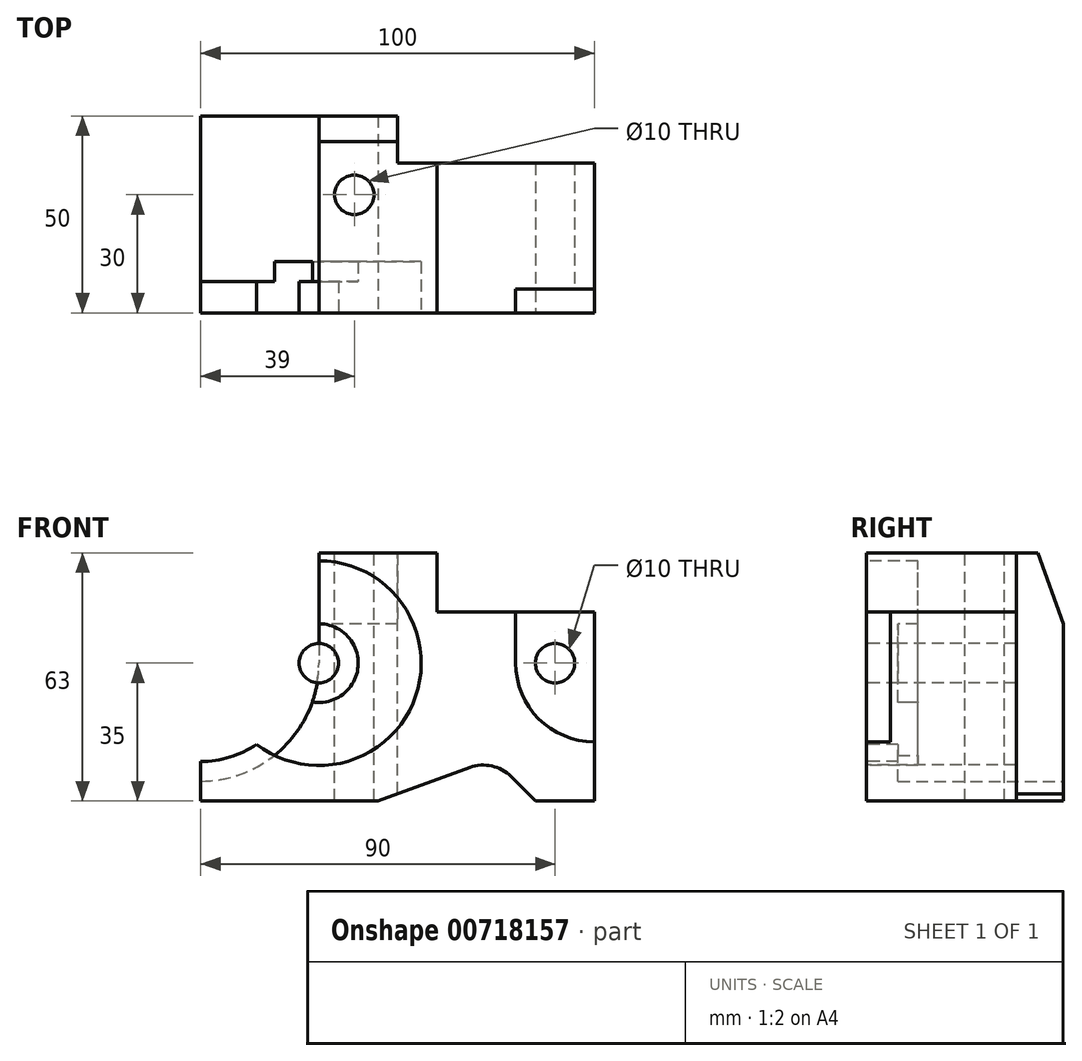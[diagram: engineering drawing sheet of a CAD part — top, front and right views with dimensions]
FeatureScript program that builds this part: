
annotation { "Feature Type Name" : "Feature", "Feature Type Description" : "" }
export const myFeature = defineFeature(function(context is Context, id is Id, definition is map)
    precondition{}
    {
        {
            var Q0;
            Q0=qCreatedBy(makeId("Front.planeOp"),FACE);
            var sketch = newSketch(context, id + "F0", { "sketchPlane" : qUnion([Q0])});
            skLineSegment(sketch, "E0.bottom", {"start": v(0, 0) * mm, "end": v(100, 0) * mm});
            skLineSegment(sketch, "E0.top", {"start": v(0, 63) * mm, "end": v(100, 63) * mm});
            skLineSegment(sketch, "E0.left", {"start": v(0, 0) * mm, "end": v(0, 63) * mm});
            skLineSegment(sketch, "E0.right", {"start": v(100, 0) * mm, "end": v(100, 63) * mm});
            skSolve(sketch);
        }
        {
            var Q0;
            Q0 = qSketchRegion(id + "F0", true);
            extrude(context, id + "F1", {"entities" : qUnion([Q0]), "depth" : 50 * mm, "offsetDistance" : 25 * mm});
        }
        {
            var Q0;
            Q0=makeQuery(id+"F1.opExtrude","CAP_FACE",FACE,{"disambiguationData":[OSD([sQuery(id+"F0.wireOp",EDGE,"E0.bottom"),sQuery(id+"F0.wireOp",EDGE,"E0.top"),sQuery(id+"F0.wireOp",EDGE,"E0.left"),sQuery(id+"F0.wireOp",EDGE,"E0.right")])],"isStart":false});
            var sketch = newSketch(context, id + "F2", { "sketchPlane" : qUnion([Q0])});
            skLineSegment(sketch, "E1.bottom", {"start": v(100, 63) * mm, "end": v(60, 63) * mm});
            skLineSegment(sketch, "E1.top", {"start": v(100, 48) * mm, "end": v(60, 48) * mm});
            skLineSegment(sketch, "E1.left", {"start": v(100, 63) * mm, "end": v(100, 48) * mm});
            skLineSegment(sketch, "E1.right", {"start": v(60, 63) * mm, "end": v(60, 48) * mm});
            skSolve(sketch);
        }
        {
            var Q0;
            Q0 = qSketchRegion(id + "F2", true);
            extrude(context, id + "F3", {"entities" : qUnion([Q0]), "operationType" : NewBodyOperationType.REMOVE, "endBound" : BoundingType.THROUGH_ALL, "oppositeDirection" : true, "depth" : 25 * mm, "offsetDistance" : 25 * mm});
        }
        {
            var Q0;
            Q0=makeQuery(id+"F1.opExtrude","CAP_FACE",FACE,{"disambiguationData":[OSD([sQuery(id+"F0.wireOp",EDGE,"E0.bottom"),sQuery(id+"F0.wireOp",EDGE,"E0.top"),sQuery(id+"F0.wireOp",EDGE,"E0.left"),sQuery(id+"F0.wireOp",EDGE,"E0.right")])],"isStart":false});
            var sketch = newSketch(context, id + "F4", { "sketchPlane" : qUnion([Q0])});
            skCircle(sketch, "E2", {"center": v(90, 35) * mm, "radius": 5 * mm});
            skSolve(sketch);
        }
        {
            var Q0;
            Q0 = qSketchRegion(id + "F4", true);
            extrude(context, id + "F5", {"entities" : qUnion([Q0]), "operationType" : NewBodyOperationType.REMOVE, "endBound" : BoundingType.THROUGH_ALL, "oppositeDirection" : true, "depth" : 25 * mm, "offsetDistance" : 25 * mm});
        }
        {
            var Q0;
            Q0=makeQuery(id+"F1.opExtrude","CAP_FACE",FACE,{"disambiguationData":[OSD([sQuery(id+"F0.wireOp",EDGE,"E0.bottom"),sQuery(id+"F0.wireOp",EDGE,"E0.top"),sQuery(id+"F0.wireOp",EDGE,"E0.left"),sQuery(id+"F0.wireOp",EDGE,"E0.right")])],"isStart":false});
            var sketch = newSketch(context, id + "F6", { "sketchPlane" : qUnion([Q0])});
            skLineSegment(sketch, "E3", {"start": v(45, 0) * mm, "end": v(68.34, 8.5) * mm});
            skArc(sketch, "E4", {"start": v(78.83, 6.17) * mm, "mid": v(73.92, 8.86) * mm, "end": v(68.34, 8.5) * mm});
            skLineSegment(sketch, "E5", {"start": v(78.83, 6.17) * mm, "end": v(85, 0) * mm});
            skLineSegment(sketch, "E6", {"start": v(45, 0) * mm, "end": v(85, 0) * mm});
            skSolve(sketch);
        }
        {
            var Q0;
            Q0 = qSketchRegion(id + "F6", true);
            extrude(context, id + "F7", {"entities" : qUnion([Q0]), "operationType" : NewBodyOperationType.REMOVE, "endBound" : BoundingType.THROUGH_ALL, "oppositeDirection" : true, "depth" : 25 * mm, "offsetDistance" : 25 * mm});
        }
        {
            var Q0;
            Q0=makeQuery(id+"F1.opExtrude","CAP_FACE",FACE,{"disambiguationData":[OSD([sQuery(id+"F0.wireOp",EDGE,"E0.bottom"),sQuery(id+"F0.wireOp",EDGE,"E0.top"),sQuery(id+"F0.wireOp",EDGE,"E0.left"),sQuery(id+"F0.wireOp",EDGE,"E0.right")])],"isStart":false});
            var sketch = newSketch(context, id + "F8", { "sketchPlane" : qUnion([Q0])});
            skLineSegment(sketch, "E7", {"start": v(80, 48) * mm, "end": v(80, 35) * mm});
            skArc(sketch, "E8", {"start": v(80, 35) * mm, "mid": v(85.86, 20.86) * mm, "end": v(100, 15) * mm});
            skLineSegment(sketch, "E9", {"start": v(80, 48) * mm, "end": v(100, 48) * mm});
            skLineSegment(sketch, "E10", {"start": v(100, 48) * mm, "end": v(100, 15) * mm});
            skSolve(sketch);
        }
        {
            var Q0;
            Q0 = qSketchRegion(id + "F8", true);
            extrude(context, id + "F9", {"entities" : qUnion([Q0]), "operationType" : NewBodyOperationType.REMOVE, "oppositeDirection" : true, "depth" : 6 * mm, "offsetDistance" : 25 * mm});
        }
        {
            var Q0;
            Q0=makeQuery(id+"F1.opExtrude","SWEPT_FACE",FACE,{"disambiguationData":[OSD([sQuery(id+"F0.wireOp",EDGE,"E0.top")])]});
            var sketch = newSketch(context, id + "F10", { "sketchPlane" : qUnion([Q0])});
            skLineSegment(sketch, "E11.bottom", {"start": v(50, 0) * mm, "end": v(100, 0) * mm});
            skLineSegment(sketch, "E11.top", {"start": v(50, -12) * mm, "end": v(100, -12) * mm});
            skLineSegment(sketch, "E11.left", {"start": v(50, 0) * mm, "end": v(50, -12) * mm});
            skLineSegment(sketch, "E11.right", {"start": v(100, 0) * mm, "end": v(100, -12) * mm});
            skSolve(sketch);
        }
        {
            var Q0;
            Q0 = qSketchRegion(id + "F10", true);
            extrude(context, id + "F11", {"entities" : qUnion([Q0]), "operationType" : NewBodyOperationType.REMOVE, "endBound" : BoundingType.THROUGH_ALL, "oppositeDirection" : true, "depth" : 25 * mm, "offsetDistance" : 25 * mm});
        }
        {
            var Q0;
            Q0=makeQuery(id+"F1.opExtrude","CAP_FACE",FACE,{"disambiguationData":[OSD([sQuery(id+"F0.wireOp",EDGE,"E0.bottom"),sQuery(id+"F0.wireOp",EDGE,"E0.top"),sQuery(id+"F0.wireOp",EDGE,"E0.left"),sQuery(id+"F0.wireOp",EDGE,"E0.right")])],"isStart":false});
            var sketch = newSketch(context, id + "F12", { "sketchPlane" : qUnion([Q0])});
            skCircle(sketch, "E12", {"center": v(30, 35) * mm, "radius": 26 * mm});
            skCircle(sketch, "E13", {"center": v(30, 35) * mm, "radius": 10 * mm});
            skSolve(sketch);
        }
        {
            var Q0;
            Q0 = qSketchRegion(id + "F12", true);
            extrude(context, id + "F13", {"entities" : qUnion([Q0]), "operationType" : NewBodyOperationType.REMOVE, "oppositeDirection" : true, "depth" : 13 * mm, "offsetDistance" : 25 * mm});
        }
        {
            var Q0;
            Q0=makeQuery(id+"F13.boolean.opBoolean","SPLIT",FACE,{"disambiguationData":[TD([makeQuery(id+"F13.opExtrude","SWEPT_FACE",FACE,{"disambiguationData":[OSD([sQuery(id+"F12.wireOp",EDGE,"E13")])]})])],"derivedFrom":makeQuery(id+"F1.opExtrude","CAP_FACE",FACE,{"disambiguationData":[OSD([sQuery(id+"F0.wireOp",EDGE,"E0.bottom"),sQuery(id+"F0.wireOp",EDGE,"E0.top"),sQuery(id+"F0.wireOp",EDGE,"E0.left"),sQuery(id+"F0.wireOp",EDGE,"E0.right")])],"isStart":false})});
            var sketch = newSketch(context, id + "F14", { "sketchPlane" : qUnion([Q0])});
            skCircle(sketch, "E14", {"center": v(30, 35) * mm, "radius": 5 * mm});
            skCircle(sketch, "E15", {"center": v(30, 35) * mm, "radius": 10 * mm});
            skSolve(sketch);
        }
        {
            var Q0;
            Q0 = qSketchRegion(id + "F14", true);
            extrude(context, id + "F15", {"entities" : qUnion([Q0]), "operationType" : NewBodyOperationType.REMOVE, "oppositeDirection" : true, "depth" : 8 * mm, "offsetDistance" : 25 * mm});
        }
        {
            var Q0;
            {var subQ0=sQuery(id+"F0.wireOp",EDGE,"E0.bottom");var subQ1=sQuery(id+"F0.wireOp",EDGE,"E0.right");var subQ2=sQuery(id+"F0.wireOp",EDGE,"E0.top");var subQ3=sQuery(id+"F0.wireOp",EDGE,"E0.left");Q0=makeQuery(id+"F13.boolean.opBoolean","SPLIT",FACE,{"disambiguationData":[TD([makeQuery(id+"F1.opExtrude","SWEPT_FACE",FACE,{"disambiguationData":[OSD([subQ0])]})])],"derivedFrom":makeQuery(id+"F1.opExtrude","CAP_FACE",FACE,{"disambiguationData":[OSD([subQ0,subQ2,subQ3,subQ1])],"isStart":false})});}
            var sketch = newSketch(context, id + "F16", { "sketchPlane" : qUnion([Q0])});
            skArc(sketch, "E16", {"start": v(0, 10) * mm, "mid": v(7.4, 11.12) * mm, "end": v(14.15, 14.39) * mm});
            skLineSegment(sketch, "E17", {"start": v(0, 10) * mm, "end": v(0, 35) * mm});
            skArc(sketch, "E18", {"start": v(30, 61) * mm, "mid": v(5.38, 43.37) * mm, "end": v(14.15, 14.39) * mm});
            skPoint(sketch, "E19.end.orphan", {"position": v(30, 63) * mm});
            skLineSegment(sketch, "E20", {"start": v(30, 63) * mm, "end": v(0, 63) * mm});
            skLineSegment(sketch, "E21", {"start": v(0, 63) * mm, "end": v(0, 35) * mm});
            skLineSegment(sketch, "E22", {"start": v(30, 61) * mm, "end": v(30, 63) * mm});
            skSolve(sketch);
        }
        {
            var Q0;
            Q0 = qSketchRegion(id + "F16", true);
            var Q1;
            Q1=makeQuery(id+"F13.boolean.opBoolean","COPY",FACE,{"derivedFrom":makeQuery(id+"F13.opExtrude","CAP_FACE",FACE,{"disambiguationData":[OSD([sQuery(id+"F12.wireOp",EDGE,"E12"),sQuery(id+"F12.wireOp",EDGE,"E13")])],"isStart":false})});
            extrude(context, id + "F17", {"entities" : qUnion([Q0]), "operationType" : NewBodyOperationType.REMOVE, "oppositeDirection" : true, "depth" : 8 * mm, "endBoundEntityFace" : qUnion([Q1]), "offsetDistance" : 25 * mm});
        }
        {
            var Q0;
            Q0=makeQuery(id+"F1.opExtrude","CAP_FACE",FACE,{"disambiguationData":[OSD([sQuery(id+"F0.wireOp",EDGE,"E0.bottom"),sQuery(id+"F0.wireOp",EDGE,"E0.top"),sQuery(id+"F0.wireOp",EDGE,"E0.left"),sQuery(id+"F0.wireOp",EDGE,"E0.right")])],"isStart":true});
            var sketch = newSketch(context, id + "F18", { "sketchPlane" : qUnion([Q0])});
            skArc(sketch, "E23", {"start": v(-30, 35) * mm, "mid": v(-21.21, 13.79) * mm, "end": v(0, 5) * mm});
            skLineSegment(sketch, "E24", {"start": v(0, 63) * mm, "end": v(0, 5) * mm});
            skLineSegment(sketch, "E25", {"start": v(-30, 63) * mm, "end": v(0, 63) * mm});
            skPoint(sketch, "E26", {"position": v(0, 31.5) * mm});
            skCircle(sketch, "E27", {"center": v(-30, 35) * mm, "radius": 5 * mm, "construction": true});
            skLineSegment(sketch, "E28", {"start": v(-30, 63) * mm, "end": v(-30, 35) * mm});
            skSolve(sketch);
        }
        {
            var Q0;
            Q0 = qSketchRegion(id + "F18", true);
            var Q1;
            {var subQ0=sQuery(id+"F0.wireOp",EDGE,"E0.bottom");var subQ1=sQuery(id+"F0.wireOp",EDGE,"E0.right");var subQ2=sQuery(id+"F0.wireOp",EDGE,"E0.top");var subQ3=sQuery(id+"F0.wireOp",EDGE,"E0.left");Q1=makeQuery(id+"F13.boolean.opBoolean","SPLIT",FACE,{"disambiguationData":[TD([makeQuery(id+"F1.opExtrude","SWEPT_FACE",FACE,{"disambiguationData":[OSD([subQ0])]})])],"derivedFrom":makeQuery(id+"F1.opExtrude","CAP_FACE",FACE,{"disambiguationData":[OSD([subQ0,subQ2,subQ3,subQ1])],"isStart":false})});}
            extrude(context, id + "F19", {"entities" : qUnion([Q0]), "operationType" : NewBodyOperationType.REMOVE, "endBound" : BoundingType.UP_TO_SURFACE, "oppositeDirection" : true, "depth" : 25 * mm, "endBoundEntityFace" : qUnion([Q1]), "hasOffset" : true, "offsetDistance" : 8 * mm});
        }
        {
            var Q0;
            Q0=makeQuery(id+"F19.boolean.opBoolean","MERGE",FACE,{"derivedFrom":[makeQuery(id+"F17.boolean.opBoolean","COPY",FACE,{"derivedFrom":makeQuery(id+"F17.opExtrude","SWEPT_FACE",FACE,{"disambiguationData":[OSD([sQuery(id+"F16.wireOp",EDGE,"E22")])]})}),makeQuery(id+"F19.opExtrude","SWEPT_FACE",FACE,{"disambiguationData":[OSD([sQuery(id+"F18.wireOp",EDGE,"uyzwTYRJ-YWOw-MWPG-6wrV-07xEwNOWze3L")])]})]});
            var sketch = newSketch(context, id + "F20", { "sketchPlane" : qUnion([Q0])});
            skLineSegment(sketch, "E29", {"start": v(6.55, 63) * mm, "end": v(0, 45) * mm});
            skLineSegment(sketch, "E30", {"start": v(0, 45) * mm, "end": v(0, 63) * mm});
            skLineSegment(sketch, "E31", {"start": v(0, 63) * mm, "end": v(6.55, 63) * mm});
            skSolve(sketch);
        }
        {
            var Q0;
            Q0 = qSketchRegion(id + "F20", true);
            extrude(context, id + "F21", {"entities" : qUnion([Q0]), "operationType" : NewBodyOperationType.REMOVE, "endBound" : BoundingType.THROUGH_ALL, "oppositeDirection" : true, "depth" : 25 * mm, "offsetDistance" : 25 * mm});
        }
        {
            var Q0;
            Q0=makeQuery(id+"F1.opExtrude","SWEPT_FACE",FACE,{"disambiguationData":[OSD([sQuery(id+"F0.wireOp",EDGE,"E0.top")])]});
            var sketch = newSketch(context, id + "F22", { "sketchPlane" : qUnion([Q0])});
            skCircle(sketch, "E32", {"center": v(39, -20) * mm, "radius": 5 * mm});
            skSolve(sketch);
        }
        {
            var Q0;
            Q0 = qSketchRegion(id + "F22", true);
            extrude(context, id + "F23", {"entities" : qUnion([Q0]), "operationType" : NewBodyOperationType.REMOVE, "endBound" : BoundingType.THROUGH_ALL, "oppositeDirection" : true, "depth" : 25 * mm, "offsetDistance" : 25 * mm});
        }
    });
